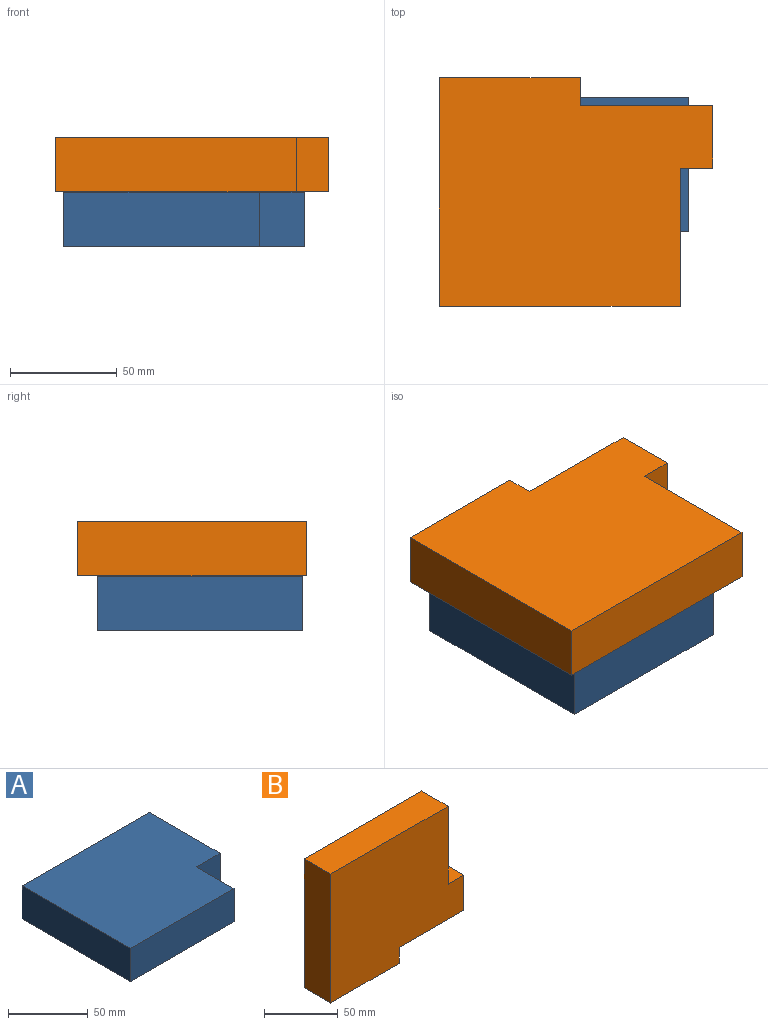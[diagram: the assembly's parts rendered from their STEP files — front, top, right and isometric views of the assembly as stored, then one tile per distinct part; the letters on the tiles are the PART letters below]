
ASSEMBLY  parts=2 mates=1
PART A: 8 faces, bbox 112.6x96.1x25.4 mm
  f0: plane 112.63x25.4mm, normal (0,1,0), area 2860.8mm2, adj f1,f5,f6,f7
  f1: plane 96.05x25.4mm, normal (-1,0,0), area 2439.8mm2, adj f0,f2,f6,f7
  f2: plane 91.59x25.4mm, normal (0,-1,0), area 2326.4mm2, adj f1,f3,f6,f7
  f3: plane 33.36x25.4mm, normal (1,0,0), area 847.4mm2, adj f2,f4,f6,f7
  f4: plane 25.4x21.04mm, normal (0,-1,0), area 534.4mm2, adj f3,f5,f6,f7
  f5: plane 62.69x25.4mm, normal (1,0,0), area 1592.3mm2, adj f0,f4,f6,f7
  f6: plane 112.63x96.05mm, normal (0,0,1), area 10116.7mm2, adj f0,f1,f2,f3,f4,f5
  f7: plane 112.63x96.05mm, normal (0,0,-1), area 10116.7mm2, adj f0,f1,f2,f3,f4,f5
PART B: 10 faces, bbox 128x25.4x107.1 mm
  f0: plane 112.85x25.4mm, normal (0,0,1), area 2866.3mm2, adj f1,f7,f8,f9
  f1: plane 107.11x25.4mm, normal (-1,0,0), area 2720.6mm2, adj f0,f2,f8,f9
  f2: plane 66.04x25.4mm, normal (0,0,-1), area 1677.5mm2, adj f1,f3,f8,f9
  f3: plane 25.4x13.13mm, normal (1,0,0), area 333.6mm2, adj f2,f4,f8,f9
  f4: plane 61.97x25.4mm, normal (0,0,-1), area 1574.1mm2, adj f3,f5,f8,f9
  f5: plane 29.23x25.4mm, normal (1,0,0), area 742.4mm2, adj f4,f6,f8,f9
  f6: plane 25.4x15.17mm, normal (0,0,1), area 385.3mm2, adj f5,f7,f8,f9
  f7: plane 64.75x25.4mm, normal (1,0,0), area 1644.6mm2, adj f0,f6,f8,f9
  f8: plane 128.02x107.11mm, normal (0,-1,0), area 11915.8mm2, adj f0,f1,f2,f3,f4,f5,f6,f7
  f9: plane 128.02x107.11mm, normal (0,1,0), area 11915.8mm2, adj f0,f1,f2,f3,f4,f5,f6,f7
PLACE A t=(-60.65,-69.15,-84.38)mm
PLACE B rot(axis=(1,0,0),90deg) t=(-59.59,-90.5,-33.58)mm
MATE fastened B.f8 <-> A.f6  axis (0,0,-1) through (-60.16,-78.51,-58.98)mm
